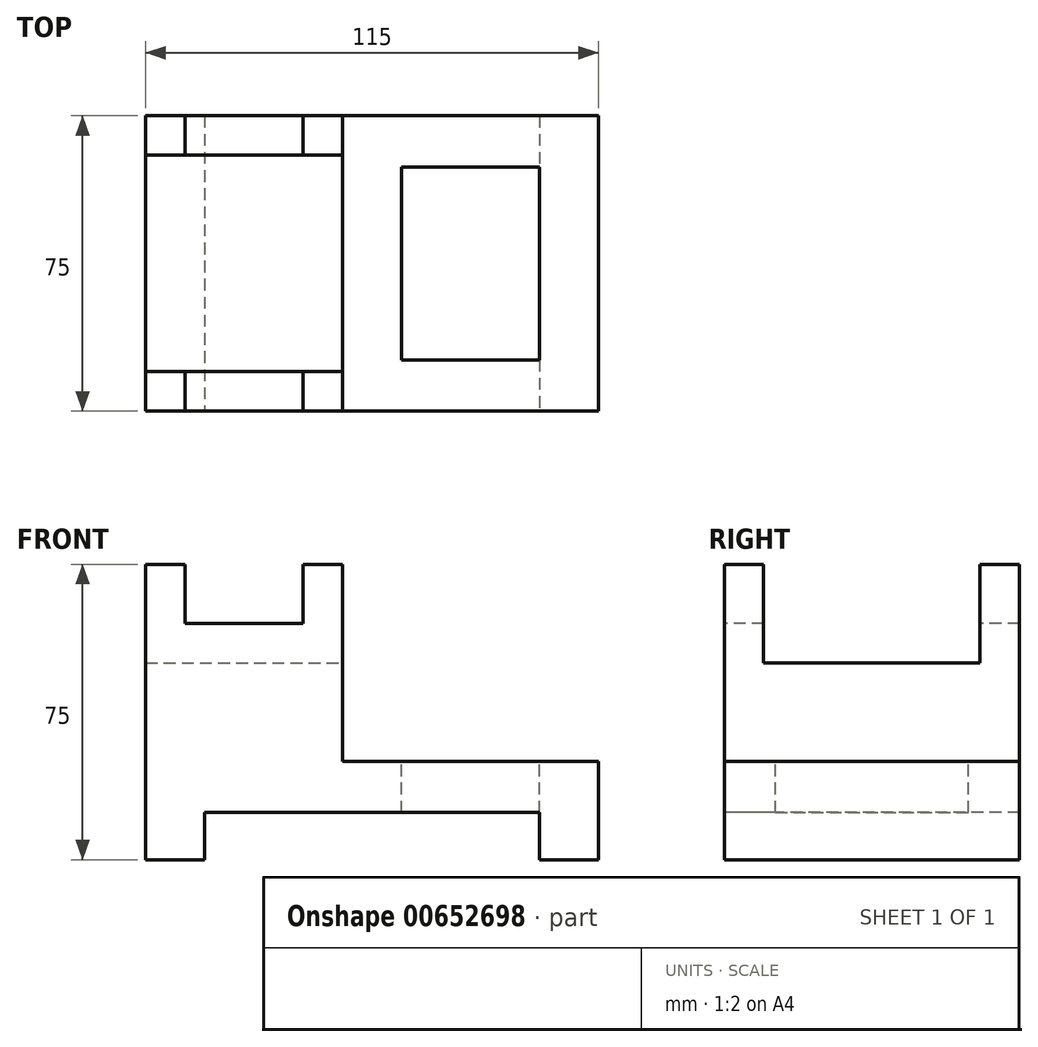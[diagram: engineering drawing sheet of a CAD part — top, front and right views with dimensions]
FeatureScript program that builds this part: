
annotation { "Feature Type Name" : "Feature", "Feature Type Description" : "" }
export const myFeature = defineFeature(function(context is Context, id is Id, definition is map)
    precondition{}
    {
        {
            var Q0;
            Q0=qCreatedBy(makeId("Top.planeOp"),FACE);
            var sketch = newSketch(context, id + "F0", { "sketchPlane" : qUnion([Q0])});
            skLineSegment(sketch, "E0.bottom", {"start": v(-55.44, -46.07) * mm, "end": v(59.56, -46.07) * mm});
            skLineSegment(sketch, "E0.top", {"start": v(-55.44, 28.93) * mm, "end": v(59.56, 28.93) * mm});
            skLineSegment(sketch, "E0.left", {"start": v(-55.44, -46.07) * mm, "end": v(-55.44, 28.93) * mm});
            skLineSegment(sketch, "E0.right", {"start": v(59.56, -46.07) * mm, "end": v(59.56, 28.93) * mm});
            skSolve(sketch);
        }
        {
            var Q0;
            Q0 = qSketchRegion(id + "F0", true);
            extrude(context, id + "F1", {"entities" : qUnion([Q0]), "depth" : 25 * mm, "offsetDistance" : 25 * mm});
        }
        {
            var Q0;
            Q0 = qSketchRegion(id + "F0", true);
            extrude(context, id + "F2", {"entities" : qUnion([Q0]), "operationType" : NewBodyOperationType.ADD, "depth" : 75 * mm, "offsetDistance" : 25 * mm});
        }
        {
            var Q0;
            {var subQ0=sQuery(id+"F0.wireOp",EDGE,"E0.bottom");Q0=makeQuery(id+"F2.boolean.opBoolean","MERGE",FACE,{"derivedFrom":[makeQuery(id+"F1.opExtrude","SWEPT_FACE",FACE,{"disambiguationData":[OSD([subQ0])]}),makeQuery(id+"F2.opExtrude","SWEPT_FACE",FACE,{"disambiguationData":[OSD([subQ0])]})]});}
            var sketch = newSketch(context, id + "F3", { "sketchPlane" : qUnion([Q0])});
            skLineSegment(sketch, "E1", {"start": v(-55.44, 75) * mm, "end": v(-45.44, 75) * mm});
            skLineSegment(sketch, "E2", {"start": v(-45.44, 75) * mm, "end": v(-45.44, 60) * mm});
            skLineSegment(sketch, "E3", {"start": v(-45.44, 60) * mm, "end": v(-11.4, 60) * mm});
            skLineSegment(sketch, "E4", {"start": v(-11.4, 60) * mm, "end": v(-11.4, 75) * mm});
            skLineSegment(sketch, "E5", {"start": v(-11.4, 75) * mm, "end": v(-1.4, 75) * mm});
            skLineSegment(sketch, "E6", {"start": v(-1.4, 0) * mm, "end": v(-40.44, 0) * mm});
            skLineSegment(sketch, "E7", {"start": v(-40.44, 0) * mm, "end": v(-40.44, 12) * mm});
            skLineSegment(sketch, "E8", {"start": v(-40.44, 12) * mm, "end": v(44.56, 12) * mm});
            skLineSegment(sketch, "E9", {"start": v(44.56, 12) * mm, "end": v(44.56, 0) * mm});
            skSolve(sketch);
        }
        {
            var Q0;
            Q0 = qSketchRegion(id + "F3", true);
            var Q1;
            {var subQ1=sQuery(id+"F3.wireOp",EDGE,"E6");Q1=makeQuery(id+"F3.imprint","IMPRINT",FACE,{"disambiguationData":[TD([[makeQuery(id+"F3.imprint","IMPRINT",EDGE,{"derivedFrom":subQ1}),1.0]])]});}
            extrude(context, id + "F4", {"entities" : qUnion([Q0, Q1]), "operationType" : NewBodyOperationType.REMOVE, "endBound" : BoundingType.THROUGH_ALL, "oppositeDirection" : true, "depth" : 25 * mm, "offsetDistance" : 25 * mm});
        }
        {
            var Q0;
            Q0=makeQuery(id+"F2.opExtrude","CAP_FACE",FACE,{"disambiguationData":[OSD([sQuery(id+"F0.wireOp",EDGE,"E0.bottom"),sQuery(id+"F0.wireOp",EDGE,"E0.top"),sQuery(id+"F0.wireOp",EDGE,"E0.left"),sQuery(id+"F0.wireOp",EDGE,"E0.right")])],"isStart":false});
            var sketch = newSketch(context, id + "F5", { "sketchPlane" : qUnion([Q0])});
            skLineSegment(sketch, "E10", {"start": v(-55.44, 18.93) * mm, "end": v(-45.44, 18.93) * mm});
            skLineSegment(sketch, "E11", {"start": v(-45.44, 18.93) * mm, "end": v(-45.44, 28.93) * mm});
            skLineSegment(sketch, "E12", {"start": v(-73.73, -8.57) * mm, "end": v(86.16, -8.57) * mm, "construction": true});
            skPoint(sketch, "E12.startSnap0", {"position": v(-55.44, -8.57) * mm});
            skPoint(sketch, "E13.endSnap0", {"position": v(2.06, 28.93) * mm});
            skLineSegment(sketch, "E14.MirrorCS", {"start": v(-55.44, -36.07) * mm, "end": v(-45.44, -36.07) * mm});
            skLineSegment(sketch, "E15.MirrorCS", {"start": v(-45.44, -36.07) * mm, "end": v(-45.44, -46.07) * mm});
            skPoint(sketch, "E16.middle", {"position": v(38.34, -8.57) * mm});
            skLineSegment(sketch, "E17", {"start": v(-5.44, 37.7) * mm, "end": v(-5.44, -53.96) * mm});
            skLineSegment(sketch, "E18", {"start": v(-15.44, 28.93) * mm, "end": v(-15.44, 18.93) * mm});
            skLineSegment(sketch, "E19", {"start": v(-15.44, 18.93) * mm, "end": v(-5.44, 18.93) * mm});
            skLineSegment(sketch, "E20", {"start": v(-5.44, -36.07) * mm, "end": v(-15.44, -36.07) * mm});
            skLineSegment(sketch, "E21", {"start": v(-15.44, -36.07) * mm, "end": v(-15.44, -46.07) * mm});
            skSolve(sketch);
        }
        {
            var Q0;
            {var subQ0=makeQuery(id+"F2.opExtrude","CAP_EDGE",EDGE,{"disambiguationData":[OSD([sQuery(id+"F0.wireOp",EDGE,"E0.right")])],"isStart":false});Q0=makeQuery(id+"F5.imprint","IMPRINT",FACE,{"disambiguationData":[TD([[makeQuery(id+"F5.imprint","IMPRINT",EDGE,{"derivedFrom":subQ0}),1.0]])]});}
            extrude(context, id + "F6", {"entities" : qUnion([Q0]), "operationType" : NewBodyOperationType.REMOVE, "oppositeDirection" : true, "depth" : 50 * mm, "offsetDistance" : 25 * mm});
        }
        {
            var Q0;
            Q0=makeQuery(id+"F6.boolean.opBoolean","COPY",FACE,{"derivedFrom":makeQuery(id+"F6.opExtrude","SWEPT_FACE",FACE,{"disambiguationData":[OSD([sQuery(id+"F5.wireOp",EDGE,"E17")])]})});
            var sketch = newSketch(context, id + "F7", { "sketchPlane" : qUnion([Q0])});
            skLineSegment(sketch, "E22", {"start": v(-46.07, 75) * mm, "end": v(-36.07, 75) * mm});
            skLineSegment(sketch, "E23", {"start": v(-36.07, 75) * mm, "end": v(-36.07, 50) * mm});
            skLineSegment(sketch, "E24", {"start": v(-36.07, 50) * mm, "end": v(18.93, 50) * mm});
            skLineSegment(sketch, "E25", {"start": v(18.93, 50) * mm, "end": v(18.93, 75) * mm});
            skLineSegment(sketch, "E26", {"start": v(18.93, 75) * mm, "end": v(28.93, 75) * mm});
            skLineSegment(sketch, "E27", {"start": v(28.93, 75) * mm, "end": v(28.93, 25) * mm});
            skLineSegment(sketch, "E28", {"start": v(28.93, 25) * mm, "end": v(-46.07, 25) * mm});
            skLineSegment(sketch, "E29", {"start": v(-46.07, 25) * mm, "end": v(-46.07, 75) * mm});
            skSolve(sketch);
        }
        {
            var Q0;
            {var subQ0=sQuery(id+"F7.wireOp",EDGE,"E23");Q0=makeQuery(id+"F7.imprint","IMPRINT",FACE,{"disambiguationData":[TD([[makeQuery(id+"F7.imprint","IMPRINT",EDGE,{"derivedFrom":subQ0}),1.0]])]});}
            extrude(context, id + "F8", {"entities" : qUnion([Q0]), "operationType" : NewBodyOperationType.REMOVE, "endBound" : BoundingType.THROUGH_ALL, "oppositeDirection" : true, "depth" : 25 * mm, "offsetDistance" : 25 * mm});
        }
        {
            var Q0;
            Q0=makeQuery(id+"F6.boolean.opBoolean","COPY",FACE,{"derivedFrom":makeQuery(id+"F6.opExtrude","CAP_FACE",FACE,{"disambiguationData":[OSD([sQuery(id+"F0.wireOp",EDGE,"E0.bottom"),sQuery(id+"F0.wireOp",EDGE,"E0.top"),sQuery(id+"F0.wireOp",EDGE,"E0.right"),sQuery(id+"F5.wireOp",EDGE,"E17")])],"isStart":false})});
            var sketch = newSketch(context, id + "F9", { "sketchPlane" : qUnion([Q0])});
            skLineSegment(sketch, "E30.bottom", {"start": v(44.56, 15.93) * mm, "end": v(9.56, 15.93) * mm});
            skLineSegment(sketch, "E30.top", {"start": v(44.56, -33.07) * mm, "end": v(9.56, -33.07) * mm});
            skLineSegment(sketch, "E30.left", {"start": v(44.56, 15.93) * mm, "end": v(44.56, -33.07) * mm});
            skLineSegment(sketch, "E30.right", {"start": v(9.56, 15.93) * mm, "end": v(9.56, -33.07) * mm});
            skPoint(sketch, "E30.middle", {"position": v(27.06, -8.57) * mm});
            skPoint(sketch, "E30.middle.positionSnap0", {"position": v(-5.44, -8.57) * mm});
            skPoint(sketch, "E30.centerSnap0", {"position": v(-5.44, -8.57) * mm});
            skSolve(sketch);
        }
        {
            var Q0;
            Q0=makeQuery(id+"F9.imprint","IMPRINT",FACE,{"disambiguationData":[TD([[makeQuery(id+"F9.imprint","IMPRINT",EDGE,{"derivedFrom":sQuery(id+"F9.wireOp",EDGE,"E30.bottom")}),1.0]])]});
            extrude(context, id + "F10", {"entities" : qUnion([Q0]), "operationType" : NewBodyOperationType.REMOVE, "endBound" : BoundingType.THROUGH_ALL, "oppositeDirection" : true, "depth" : 25 * mm, "offsetDistance" : 25 * mm});
        }
        {
            var Q0;
            {var subQ0=sQuery(id+"F0.wireOp",EDGE,"E0.left");var subQ1=sQuery(id+"F0.wireOp",EDGE,"E0.top");Q0=makeQuery(id+"F8.boolean.opBoolean","SPLIT",FACE,{"disambiguationData":[TD([makeQuery(id+"F1.opExtrude","SWEPT_FACE",FACE,{"disambiguationData":[OSD([subQ1])]})])],"derivedFrom":makeQuery(id+"F2.opExtrude","CAP_FACE",FACE,{"disambiguationData":[OSD([sQuery(id+"F0.wireOp",EDGE,"E0.bottom"),subQ1,subQ0,sQuery(id+"F0.wireOp",EDGE,"E0.right")])],"isStart":false})});}
            var sketch = newSketch(context, id + "F11", { "sketchPlane" : qUnion([Q0])});
            skLineSegment(sketch, "E31", {"start": v(-45.44, 28.93) * mm, "end": v(-45.44, 18.93) * mm});
            skLineSegment(sketch, "E32", {"start": v(-15.44, 28.93) * mm, "end": v(-15.44, 18.93) * mm});
            skSolve(sketch);
        }
        {
            var Q0;
            {var subQ0=sQuery(id+"F11.wireOp",EDGE,"E31");Q0=makeQuery(id+"F11.imprint","IMPRINT",FACE,{"disambiguationData":[TD([[makeQuery(id+"F11.imprint","IMPRINT",EDGE,{"derivedFrom":subQ0}),1.0]])]});}
            extrude(context, id + "F12", {"entities" : qUnion([Q0]), "operationType" : NewBodyOperationType.REMOVE, "oppositeDirection" : true, "depth" : 15 * mm, "offsetDistance" : 25 * mm});
        }
        {
            var Q0;
            {var subQ0=sQuery(id+"F0.wireOp",EDGE,"E0.bottom");var subQ1=sQuery(id+"F0.wireOp",EDGE,"E0.left");Q0=makeQuery(id+"F8.boolean.opBoolean","SPLIT",FACE,{"disambiguationData":[TD([makeQuery(id+"F1.opExtrude","SWEPT_FACE",FACE,{"disambiguationData":[OSD([subQ0])]})])],"derivedFrom":makeQuery(id+"F2.opExtrude","CAP_FACE",FACE,{"disambiguationData":[OSD([subQ0,sQuery(id+"F0.wireOp",EDGE,"E0.top"),subQ1,sQuery(id+"F0.wireOp",EDGE,"E0.right")])],"isStart":false})});}
            var sketch = newSketch(context, id + "F13", { "sketchPlane" : qUnion([Q0])});
            skLineSegment(sketch, "E33", {"start": v(-45.44, -36.07) * mm, "end": v(-45.44, -46.07) * mm});
            skLineSegment(sketch, "E34", {"start": v(-15.44, -36.07) * mm, "end": v(-15.44, -46.07) * mm});
            skSolve(sketch);
        }
        {
            var Q0;
            {var subQ0=sQuery(id+"F13.wireOp",EDGE,"E33");Q0=makeQuery(id+"F13.imprint","IMPRINT",FACE,{"disambiguationData":[TD([[makeQuery(id+"F13.imprint","IMPRINT",EDGE,{"derivedFrom":subQ0}),1.0]])]});}
            extrude(context, id + "F14", {"entities" : qUnion([Q0]), "operationType" : NewBodyOperationType.REMOVE, "oppositeDirection" : true, "depth" : 15 * mm, "offsetDistance" : 25 * mm});
        }
    });
